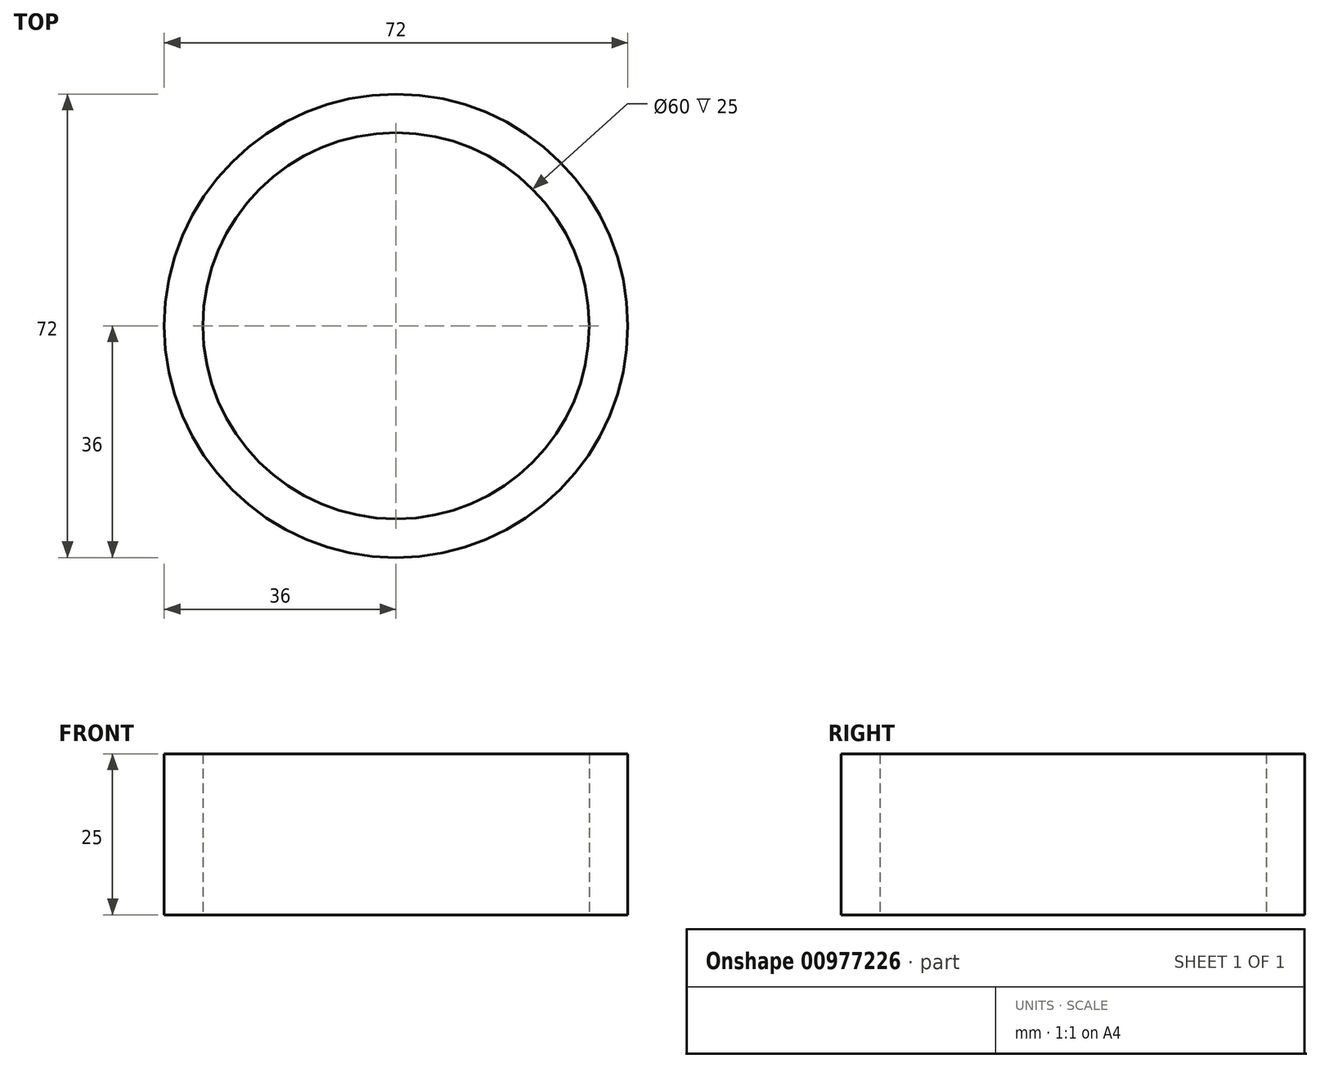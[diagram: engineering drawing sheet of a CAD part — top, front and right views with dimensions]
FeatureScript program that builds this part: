
annotation { "Feature Type Name" : "Feature", "Feature Type Description" : "" }
export const myFeature = defineFeature(function(context is Context, id is Id, definition is map)
    precondition{}
    {
        {
            var Q0;
            Q0=qCreatedBy(makeId("Top.planeOp"),FACE);
            var sketch = newSketch(context, id + "F0", { "sketchPlane" : qUnion([Q0])});
            skCircle(sketch, "E0", {"center": v(0, 0) * mm, "radius": 30 * mm});
            skCircle(sketch, "E1", {"center": v(0, 0) * mm, "radius": 36 * mm});
            skSolve(sketch);
        }
        {
            var Q0;
            Q0=makeQuery(id+"F0.imprint","IMPRINT",FACE,{"disambiguationData":[TD([[makeQuery(id+"F0.imprint","IMPRINT",EDGE,{"derivedFrom":sQuery(id+"F0.wireOp",EDGE,"E0")}),-1.0]])]});
            extrude(context, id + "F1", {"entities" : qUnion([Q0]), "depth" : 25 * mm, "offsetDistance" : 25 * mm});
        }
    });
